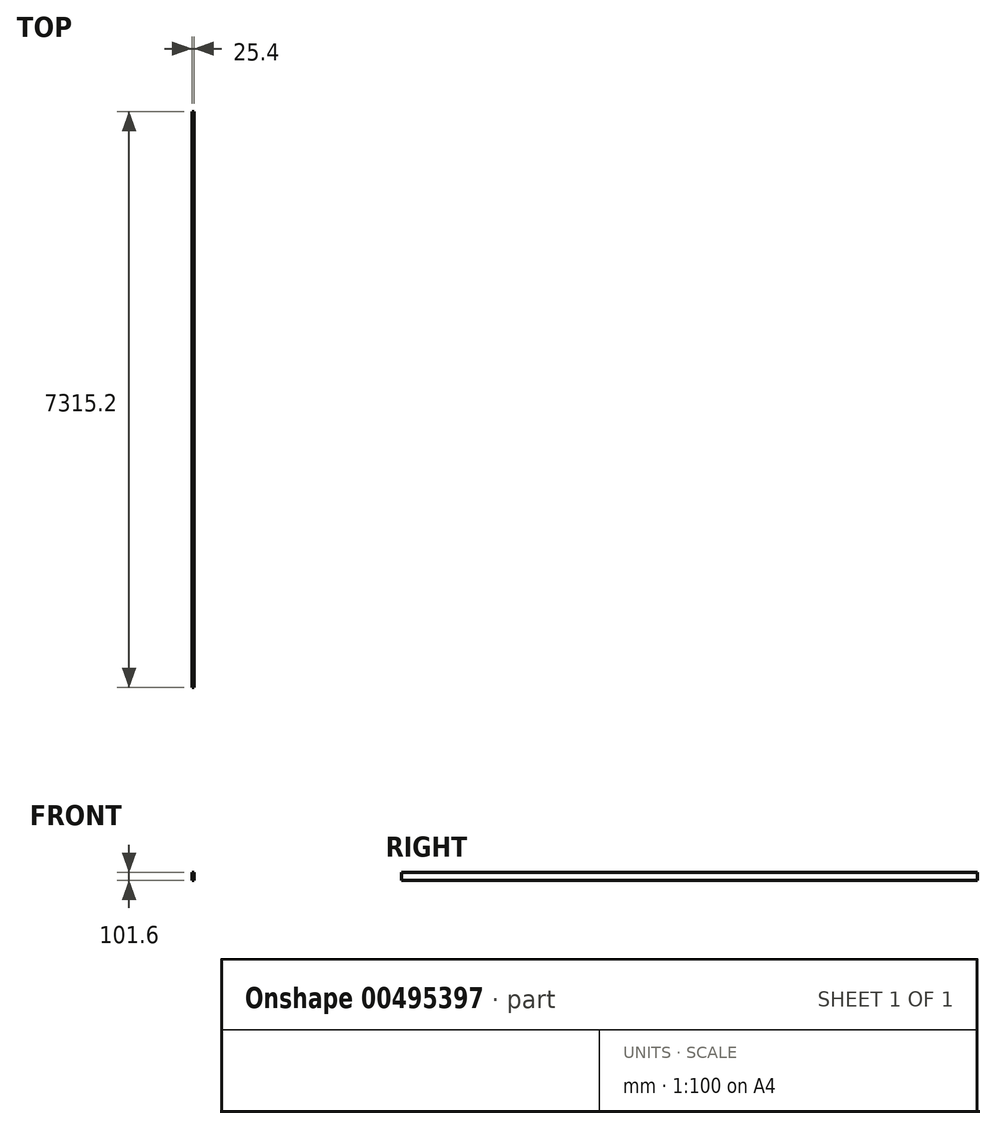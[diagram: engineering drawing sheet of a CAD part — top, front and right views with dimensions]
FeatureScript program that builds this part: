
annotation { "Feature Type Name" : "Feature", "Feature Type Description" : "" }
export const myFeature = defineFeature(function(context is Context, id is Id, definition is map)
    precondition{}
    {
        {
            var Q0;
            Q0=qCreatedBy(makeId("Front.planeOp"),FACE);
            var sketch = newSketch(context, id + "F0", { "sketchPlane" : qUnion([Q0])});
            skLineSegment(sketch, "E0.bottom", {"start": v(0, 0) * mm, "end": v(25.4, 0) * mm});
            skLineSegment(sketch, "E0.top", {"start": v(0, 101.6) * mm, "end": v(25.4, 101.6) * mm});
            skLineSegment(sketch, "E0.left", {"start": v(0, 0) * mm, "end": v(0, 101.6) * mm});
            skLineSegment(sketch, "E0.right", {"start": v(25.4, 0) * mm, "end": v(25.4, 101.6) * mm});
            skSolve(sketch);
        }
        {
            var Q0;
            Q0 = qSketchRegion(id + "F0", true);
            extrude(context, id + "F1", {"entities" : qUnion([Q0]), "depth" : 7315.2 * mm, "offsetDistance" : 25.4 * mm});
        }
    });
